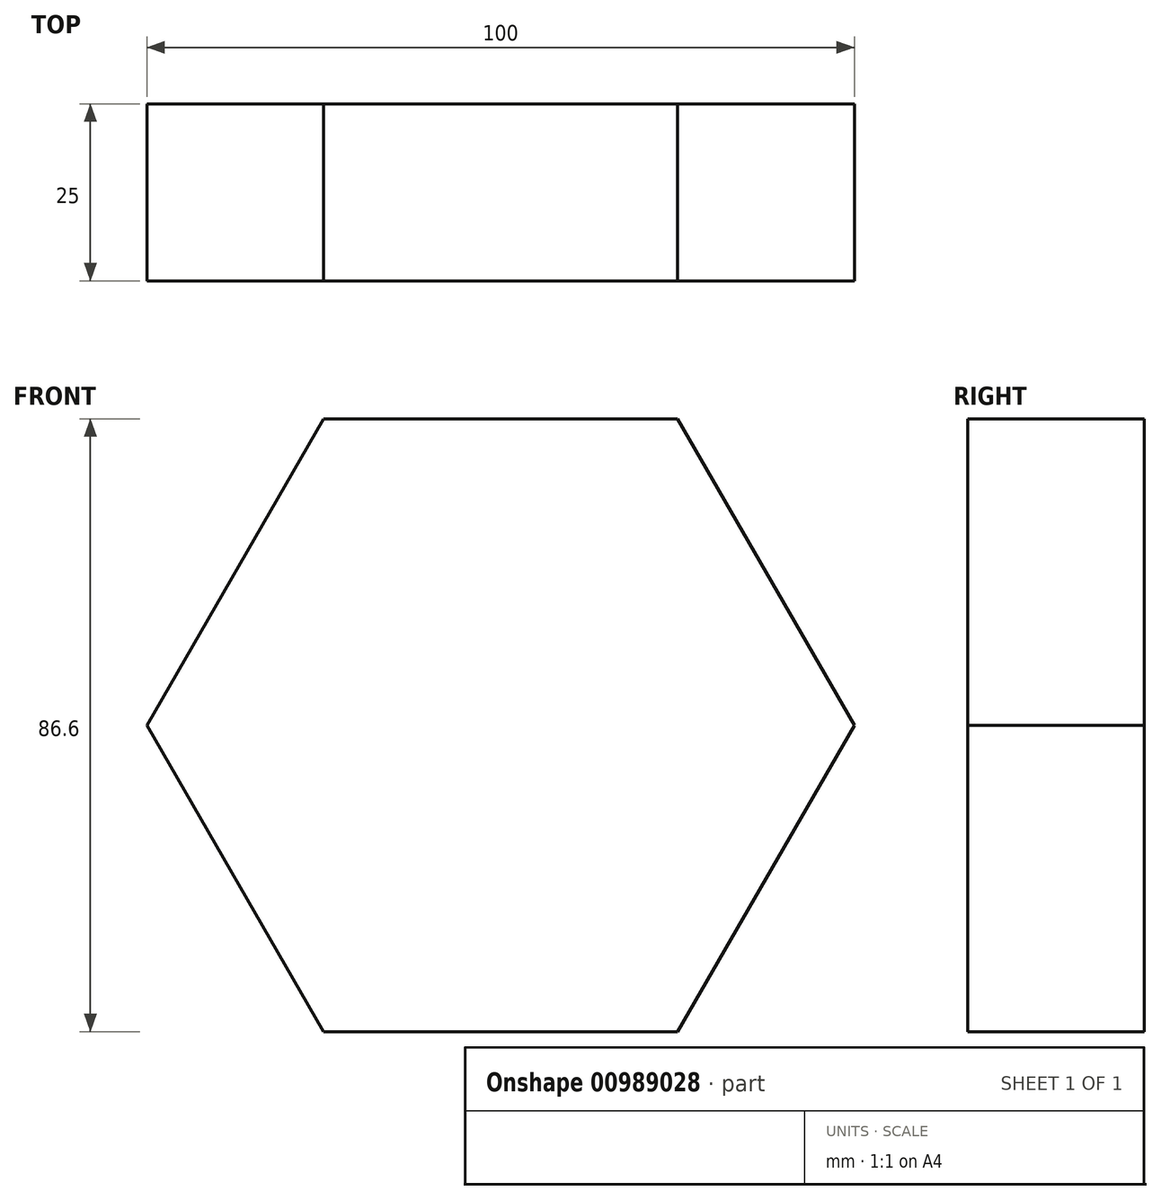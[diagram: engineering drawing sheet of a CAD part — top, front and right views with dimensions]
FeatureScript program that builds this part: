
annotation { "Feature Type Name" : "Feature", "Feature Type Description" : "" }
export const myFeature = defineFeature(function(context is Context, id is Id, definition is map)
    precondition{}
    {
        {
            var Q0;
            Q0=qCreatedBy(makeId("Front.planeOp"),FACE);
            var sketch = newSketch(context, id + "F0", { "sketchPlane" : qUnion([Q0])});
            skCircle(sketch, "E0.cCircle", {"center": v(0, 0) * mm, "radius": 43.3 * mm, "construction": true});
            skLineSegment(sketch, "E0.0", {"start": v(-25, 43.3) * mm, "end": v(25, 43.3) * mm});
            skLineSegment(sketch, "E0.1", {"start": v(25, 43.3) * mm, "end": v(50, 0) * mm});
            skLineSegment(sketch, "E0.2", {"start": v(50, 0) * mm, "end": v(25, -43.3) * mm});
            skLineSegment(sketch, "E0.3", {"start": v(25, -43.3) * mm, "end": v(-25, -43.3) * mm});
            skLineSegment(sketch, "E0.4", {"start": v(-25, -43.3) * mm, "end": v(-50, 0) * mm});
            skLineSegment(sketch, "E0.5", {"start": v(-50, 0) * mm, "end": v(-25, 43.3) * mm});
            skPoint(sketch, "E0.0.midPoint", {"position": v(0, 43.3) * mm});
            skSolve(sketch);
        }
        {
            var Q0;
            Q0=makeQuery(id+"F0.imprint","IMPRINT",FACE,{"disambiguationData":[TD([[makeQuery(id+"F0.imprint","IMPRINT",EDGE,{"derivedFrom":sQuery(id+"F0.wireOp",EDGE,"E0.0")}),-1.0]])]});
            extrude(context, id + "F1", {"entities" : qUnion([Q0]), "depth" : 25 * mm, "offsetDistance" : 25 * mm});
        }
    });
